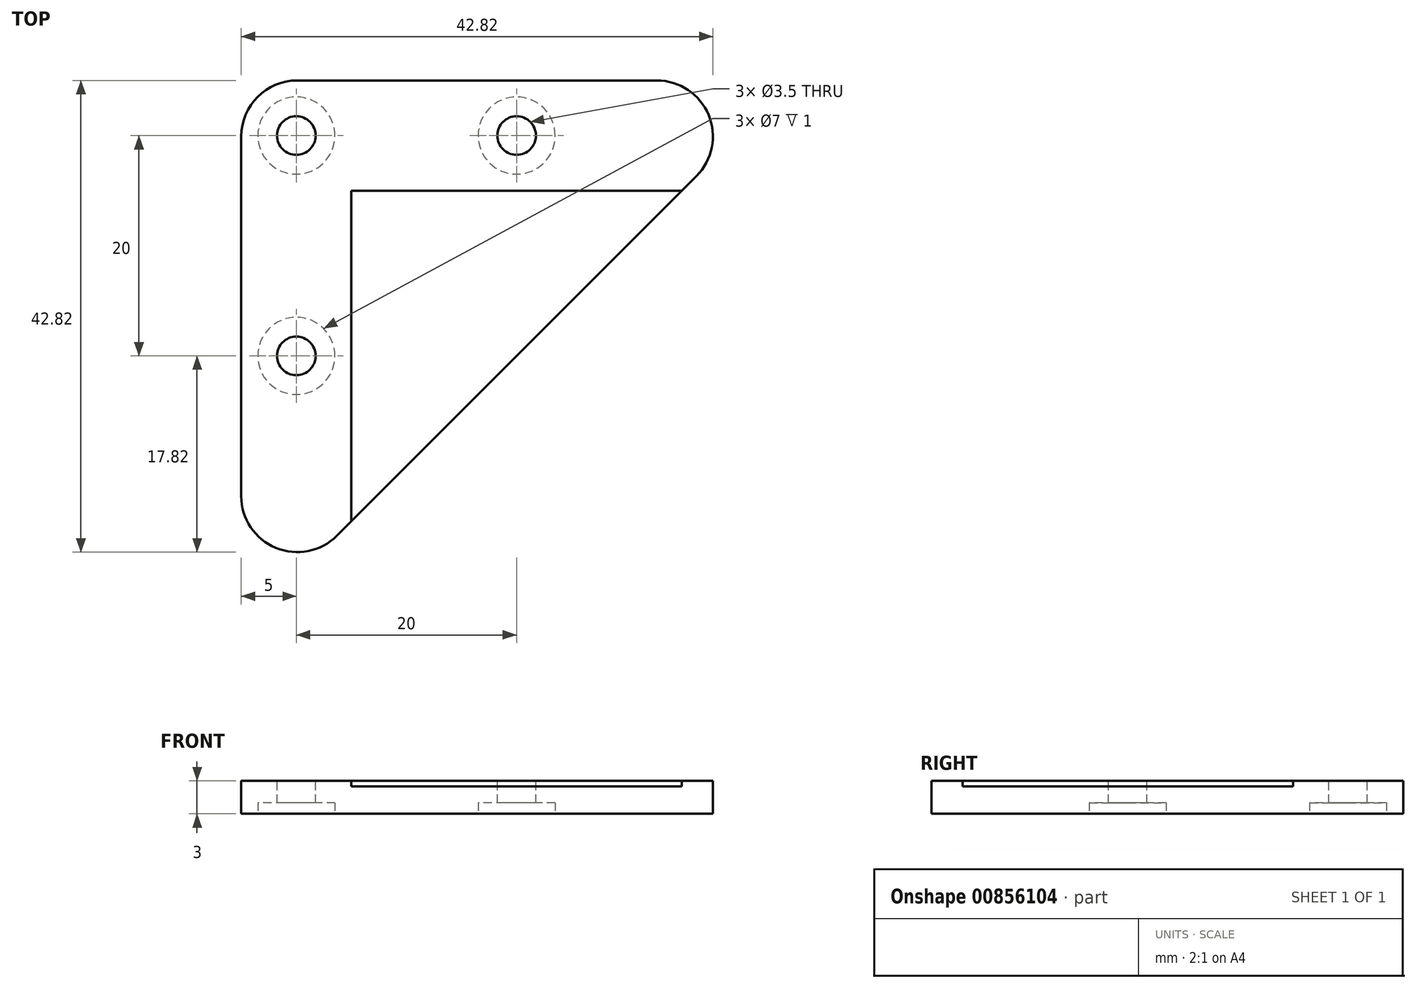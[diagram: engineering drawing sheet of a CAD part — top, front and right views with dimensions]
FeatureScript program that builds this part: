
annotation { "Feature Type Name" : "Feature", "Feature Type Description" : "" }
export const myFeature = defineFeature(function(context is Context, id is Id, definition is map)
    precondition{}
    {
        {
            var Q0;
            Q0=qCreatedBy(makeId("Top.planeOp"),FACE);
            var sketch = newSketch(context, id + "F0", { "sketchPlane" : qUnion([Q0])});
            skLineSegment(sketch, "E0.bottom", {"start": v(25, -25) * mm, "end": v(-25, -25) * mm, "construction": true});
            skLineSegment(sketch, "E0.top", {"start": v(25, 25) * mm, "end": v(-25, 25) * mm});
            skLineSegment(sketch, "E0.left", {"start": v(25, -25) * mm, "end": v(25, 25) * mm, "construction": true});
            skLineSegment(sketch, "E0.right", {"start": v(-25, -25) * mm, "end": v(-25, 25) * mm});
            skPoint(sketch, "E0.middle", {"position": v(0, 0) * mm});
            skLineSegment(sketch, "E1", {"start": v(-25, -25) * mm, "end": v(25, 25) * mm});
            skLineSegment(sketch, "E2.bottom", {"start": v(15, -15) * mm, "end": v(-15, -15) * mm, "construction": true});
            skLineSegment(sketch, "E2.top", {"start": v(15, 15) * mm, "end": v(-15, 15) * mm});
            skLineSegment(sketch, "E2.left", {"start": v(15, -15) * mm, "end": v(15, 15) * mm, "construction": true});
            skLineSegment(sketch, "E2.right", {"start": v(-15, -15) * mm, "end": v(-15, 15) * mm});
            skSolve(sketch);
        }
        {
            var Q0;
            {var subQ1=sQuery(id+"F0.wireOp",EDGE,"E0.top");Q0=makeQuery(id+"F0.imprint","IMPRINT",FACE,{"disambiguationData":[TD([[makeQuery(id+"F0.imprint","IMPRINT",EDGE,{"derivedFrom":subQ1}),1.0]])]});}
            extrude(context, id + "F1", {"entities" : qUnion([Q0]), "depth" : 3 * mm, "offsetDistance" : 25.4 * mm});
        }
        {
            var Q0;
            {var subQ0=sQuery(id+"F0.wireOp",EDGE,"E2.top");Q0=makeQuery(id+"F0.imprint","IMPRINT",FACE,{"disambiguationData":[TD([[makeQuery(id+"F0.imprint","IMPRINT",EDGE,{"derivedFrom":subQ0}),1.0]])]});}
            extrude(context, id + "F2", {"entities" : qUnion([Q0]), "operationType" : NewBodyOperationType.ADD, "depth" : 2.5 * mm, "offsetDistance" : 25.4 * mm});
        }
        {
            var Q0;
            Q0=makeQuery(id+"F1.opExtrude","CAP_FACE",FACE,{"disambiguationData":[OSD([sQuery(id+"F0.wireOp",EDGE,"E0.top"),sQuery(id+"F0.wireOp",EDGE,"E0.right"),sQuery(id+"F0.wireOp",EDGE,"E1"),sQuery(id+"F0.wireOp",EDGE,"E2.top"),sQuery(id+"F0.wireOp",EDGE,"E2.right")])],"isStart":false});
            var sketch = newSketch(context, id + "F3", { "sketchPlane" : qUnion([Q0])});
            skCircle(sketch, "E3", {"center": v(-20, 20) * mm, "radius": 1.75 * mm});
            skCircle(sketch, "E4", {"center": v(0, 20) * mm, "radius": 1.75 * mm});
            skCircle(sketch, "E5", {"center": v(-20, 0) * mm, "radius": 1.75 * mm});
            skSolve(sketch);
        }
        {
            var Q0;
            Q0=makeQuery(id+"F3.imprint","IMPRINT",FACE,{"disambiguationData":[TD([[makeQuery(id+"F3.imprint","IMPRINT",EDGE,{"derivedFrom":sQuery(id+"F3.wireOp",EDGE,"E3")}),1.0]])]});
            var Q1;
            Q1=makeQuery(id+"F3.imprint","IMPRINT",FACE,{"disambiguationData":[TD([[makeQuery(id+"F3.imprint","IMPRINT",EDGE,{"derivedFrom":sQuery(id+"F3.wireOp",EDGE,"E4")}),1.0]])]});
            var Q2;
            Q2=makeQuery(id+"F3.imprint","IMPRINT",FACE,{"disambiguationData":[TD([[makeQuery(id+"F3.imprint","IMPRINT",EDGE,{"derivedFrom":sQuery(id+"F3.wireOp",EDGE,"E5")}),1.0]])]});
            var Q3;
            Q3=sQuery(id+"F3.wireOp",EDGE,"E4");
            var Q4;
            Q4=sQuery(id+"F3.wireOp",EDGE,"E3");
            var Q5;
            Q5=sQuery(id+"F3.wireOp",EDGE,"E5");
            extrude(context, id + "F4", {"entities" : qUnion([Q0, Q1, Q2]), "operationType" : NewBodyOperationType.REMOVE, "surfaceEntities" : qUnion([Q3, Q4, Q5]), "endBound" : BoundingType.THROUGH_ALL, "oppositeDirection" : true, "depth" : 2 * mm, "offsetDistance" : 25.4 * mm});
        }
        {
            var Q0;
            {var subQ1=sQuery(id+"F0.wireOp",EDGE,"E0.top");Q0=makeQuery(id+"F0.imprint","IMPRINT",FACE,{"disambiguationData":[TD([[makeQuery(id+"F0.imprint","IMPRINT",EDGE,{"derivedFrom":subQ1}),1.0]])]});}
            var sketch = newSketch(context, id + "F5", { "sketchPlane" : qUnion([Q0])});
            skCircle(sketch, "E6", {"center": v(-20, 0) * mm, "radius": 3.5 * mm});
            skCircle(sketch, "E7", {"center": v(0, 20) * mm, "radius": 3.5 * mm});
            skCircle(sketch, "E8", {"center": v(-20, 20) * mm, "radius": 3.5 * mm});
            skSolve(sketch);
        }
        {
            var Q0;
            Q0=makeQuery(id+"F5.imprint","IMPRINT",FACE,{"disambiguationData":[TD([[makeQuery(id+"F5.imprint","IMPRINT",EDGE,{"derivedFrom":sQuery(id+"F5.wireOp",EDGE,"E6")}),1.0]])]});
            var Q1;
            Q1=makeQuery(id+"F5.imprint","IMPRINT",FACE,{"disambiguationData":[TD([[makeQuery(id+"F5.imprint","IMPRINT",EDGE,{"derivedFrom":sQuery(id+"F5.wireOp",EDGE,"E8")}),1.0]])]});
            var Q2;
            Q2=makeQuery(id+"F5.imprint","IMPRINT",FACE,{"disambiguationData":[TD([[makeQuery(id+"F5.imprint","IMPRINT",EDGE,{"derivedFrom":sQuery(id+"F5.wireOp",EDGE,"E7")}),1.0]])]});
            extrude(context, id + "F6", {"entities" : qUnion([Q0, Q1, Q2]), "operationType" : NewBodyOperationType.REMOVE, "depth" : 1 * mm, "offsetDistance" : 25.4 * mm});
        }
        {
            var Q0;
            Q0=makeQuery(id+"F1.opExtrude","SWEPT_EDGE",EDGE,{"disambiguationData":[OSD([sQuery(id+"F0.wireOp",EDGE,"E0.top"),sQuery(id+"F0.wireOp",EDGE,"E1")])]});
            var Q1;
            Q1=makeQuery(id+"F1.opExtrude","SWEPT_EDGE",EDGE,{"disambiguationData":[OSD([sQuery(id+"F0.wireOp",EDGE,"E0.right"),sQuery(id+"F0.wireOp",EDGE,"E1")])]});
            var Q2;
            Q2=makeQuery(id+"F1.opExtrude","SWEPT_EDGE",EDGE,{"disambiguationData":[OSD([sQuery(id+"F0.wireOp",EDGE,"E0.top"),sQuery(id+"F0.wireOp",EDGE,"E0.right")])]});
            fillet(context, id + "F7", {"entities" : qUnion([Q0, Q1, Q2]), "radius" : 5.08 * mm, "tangentPropagation" : true, "allowEdgeOverflow" : false});
        }
    });
